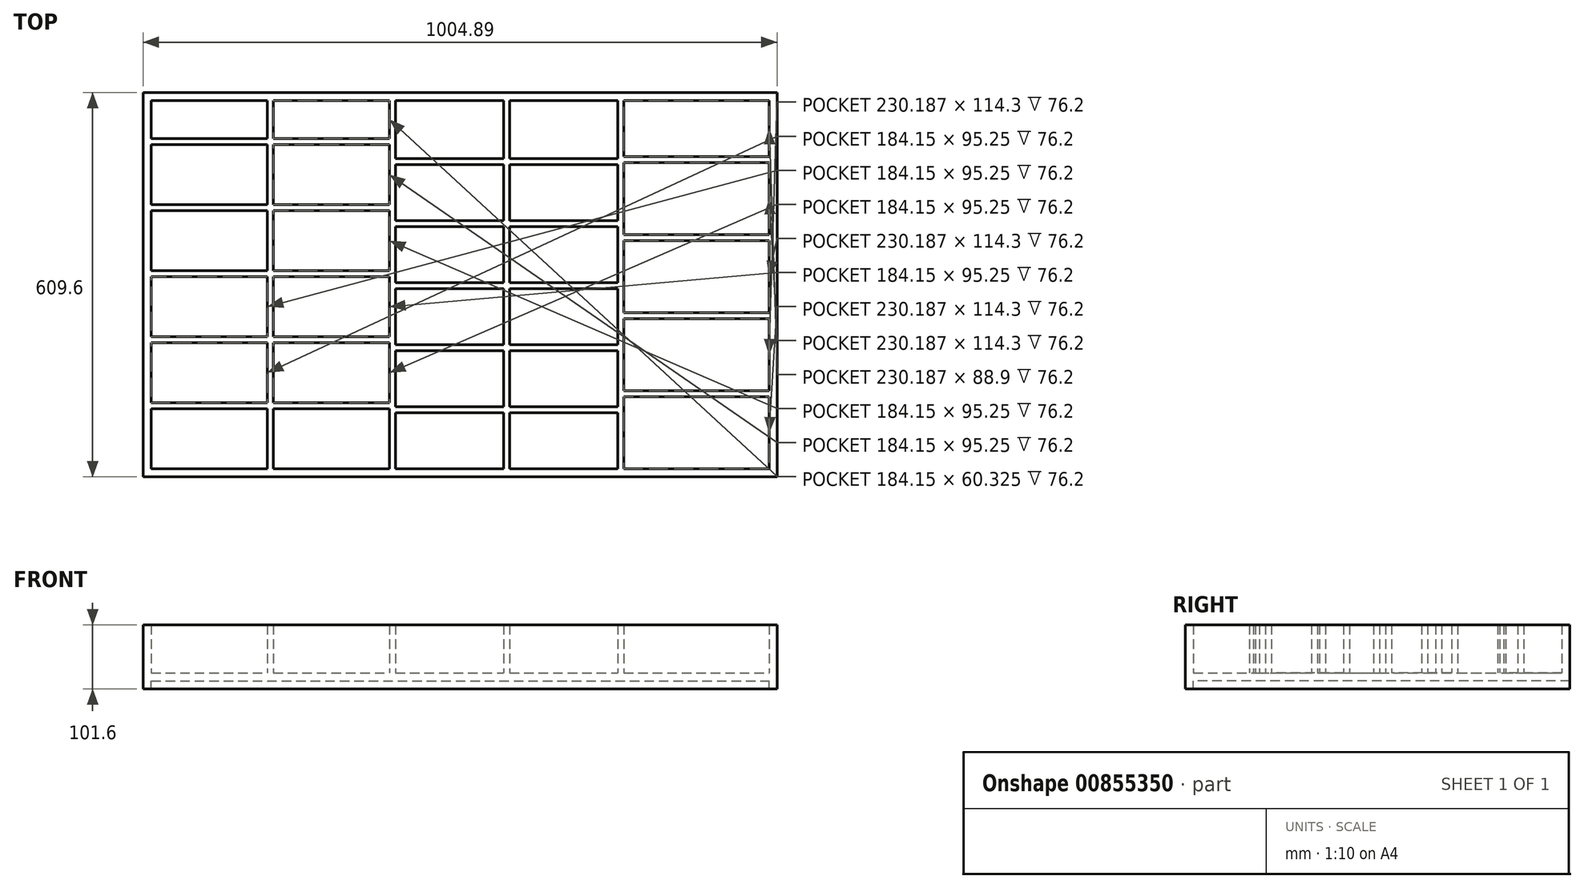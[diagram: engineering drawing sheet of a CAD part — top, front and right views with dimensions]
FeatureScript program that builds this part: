
annotation { "Feature Type Name" : "Feature", "Feature Type Description" : "" }
export const myFeature = defineFeature(function(context is Context, id is Id, definition is map)
    precondition{}
    {
        {
            var Q0;
            Q0=qCreatedBy(makeId("Top.planeOp"),FACE);
            var sketch = newSketch(context, id + "F0", { "sketchPlane" : qUnion([Q0])});
            skLineSegment(sketch, "E0.bottom", {"start": v(-1085.68, 199.34) * mm, "end": v(-901.53, 199.34) * mm});
            skLineSegment(sketch, "E0.top", {"start": v(-1085.68, -384.86) * mm, "end": v(-901.53, -384.86) * mm});
            skLineSegment(sketch, "E0.left", {"start": v(-1085.68, 199.34) * mm, "end": v(-1085.68, 34.24) * mm});
            skLineSegment(sketch, "E0.right", {"start": v(-106.19, 199.34) * mm, "end": v(-106.19, 110.44) * mm});
            skLineSegment(sketch, "E1", {"start": v(-892, -384.86) * mm, "end": v(-892, -289.61) * mm});
            skLineSegment(sketch, "E2", {"start": v(-707.85, -384.86) * mm, "end": v(-707.85, -289.61) * mm});
            skLineSegment(sketch, "E3", {"start": v(-526.88, -384.86) * mm, "end": v(-526.88, -295.96) * mm});
            skLineSegment(sketch, "E4", {"start": v(-345.9, -384.86) * mm, "end": v(-345.9, -295.96) * mm});
            skLineSegment(sketch, "E5.0", {"start": v(-901.53, -384.86) * mm, "end": v(-901.53, -289.61) * mm});
            skLineSegment(sketch, "E6.0", {"start": v(-698.33, -384.86) * mm, "end": v(-698.33, -295.96) * mm});
            skLineSegment(sketch, "E7.0", {"start": v(-517.35, -384.86) * mm, "end": v(-517.35, -295.96) * mm});
            skLineSegment(sketch, "E8.0", {"start": v(-336.38, -384.86) * mm, "end": v(-336.38, -270.56) * mm});
            skLineSegment(sketch, "E9.0", {"start": v(-1098.38, 212.04) * mm, "end": v(-93.49, 212.04) * mm});
            skLineSegment(sketch, "E9.1", {"start": v(-1098.38, 212.04) * mm, "end": v(-1098.38, -397.56) * mm});
            skLineSegment(sketch, "E9.2", {"start": v(-1098.38, -397.56) * mm, "end": v(-93.49, -397.56) * mm});
            skLineSegment(sketch, "E9.3", {"start": v(-93.49, 212.04) * mm, "end": v(-93.49, -397.56) * mm});
            skLineSegment(sketch, "E10", {"start": v(-1085.68, -280.09) * mm, "end": v(-901.53, -280.09) * mm});
            skLineSegment(sketch, "E11", {"start": v(-1085.68, -175.31) * mm, "end": v(-901.53, -175.31) * mm});
            skLineSegment(sketch, "E12", {"start": v(-707.85, -80.06) * mm, "end": v(-892, -80.06) * mm});
            skLineSegment(sketch, "E13", {"start": v(-1085.68, 34.24) * mm, "end": v(-901.53, 34.24) * mm});
            skLineSegment(sketch, "E14", {"start": v(-1085.68, 139.01) * mm, "end": v(-901.53, 139.01) * mm});
            skLineSegment(sketch, "E15", {"start": v(-698.33, -286.44) * mm, "end": v(-526.88, -286.44) * mm});
            skLineSegment(sketch, "E16", {"start": v(-345.9, -197.54) * mm, "end": v(-517.35, -197.54) * mm});
            skLineSegment(sketch, "E17", {"start": v(-698.33, -99.11) * mm, "end": v(-526.88, -99.11) * mm});
            skLineSegment(sketch, "E18", {"start": v(-345.9, -0.69) * mm, "end": v(-517.35, -0.69) * mm});
            skLineSegment(sketch, "E19", {"start": v(-698.33, 107.26) * mm, "end": v(-526.88, 107.26) * mm});
            skLineSegment(sketch, "E20.0", {"start": v(-698.33, 97.74) * mm, "end": v(-526.88, 97.74) * mm});
            skLineSegment(sketch, "E21.0", {"start": v(-345.9, 8.84) * mm, "end": v(-517.35, 8.84) * mm});
            skLineSegment(sketch, "E22.0", {"start": v(-698.33, -89.59) * mm, "end": v(-526.88, -89.59) * mm});
            skLineSegment(sketch, "E23.0", {"start": v(-345.9, -188.01) * mm, "end": v(-517.35, -188.01) * mm});
            skLineSegment(sketch, "E24.0", {"start": v(-698.33, -295.96) * mm, "end": v(-526.88, -295.96) * mm});
            skLineSegment(sketch, "E25.0", {"start": v(-1085.68, -289.61) * mm, "end": v(-901.53, -289.61) * mm});
            skLineSegment(sketch, "E26.0", {"start": v(-1085.68, -184.84) * mm, "end": v(-901.53, -184.84) * mm});
            skLineSegment(sketch, "E27.0", {"start": v(-707.85, -70.54) * mm, "end": v(-892, -70.54) * mm});
            skLineSegment(sketch, "E28.0", {"start": v(-1085.68, 24.71) * mm, "end": v(-901.53, 24.71) * mm});
            skLineSegment(sketch, "E29.0", {"start": v(-1085.68, 129.49) * mm, "end": v(-901.53, 129.49) * mm});
            skLineSegment(sketch, "E30", {"start": v(-336.38, -270.56) * mm, "end": v(-106.19, -270.56) * mm});
            skLineSegment(sketch, "E31", {"start": v(-336.38, -137.21) * mm, "end": v(-106.19, -137.21) * mm});
            skLineSegment(sketch, "E32", {"start": v(-336.38, -13.39) * mm, "end": v(-106.19, -13.39) * mm});
            skLineSegment(sketch, "E33", {"start": v(-106.19, 100.91) * mm, "end": v(-336.38, 100.91) * mm});
            skLineSegment(sketch, "E34.0", {"start": v(-336.38, -261.04) * mm, "end": v(-106.19, -261.04) * mm});
            skLineSegment(sketch, "E35.0", {"start": v(-336.38, -146.74) * mm, "end": v(-106.19, -146.74) * mm});
            skLineSegment(sketch, "E36.0", {"start": v(-336.38, -22.91) * mm, "end": v(-106.19, -22.91) * mm});
            skLineSegment(sketch, "E37.0", {"start": v(-106.19, 110.44) * mm, "end": v(-336.38, 110.44) * mm});
            skLineSegment(sketch, "E38.trimOffspring", {"start": v(-892, 199.34) * mm, "end": v(-707.85, 199.34) * mm});
            skLineSegment(sketch, "E39.trimOffspring", {"start": v(-892, 139.01) * mm, "end": v(-892, 199.34) * mm});
            skLineSegment(sketch, "E40.trimOffspring", {"start": v(-901.53, 139.01) * mm, "end": v(-901.53, 199.34) * mm});
            skLineSegment(sketch, "E41.trimOffspring", {"start": v(-892, 139.01) * mm, "end": v(-707.85, 139.01) * mm});
            skLineSegment(sketch, "E42.trimOffspring", {"start": v(-892, 129.49) * mm, "end": v(-707.85, 129.49) * mm});
            skLineSegment(sketch, "E43.trimOffspring", {"start": v(-1085.68, 24.71) * mm, "end": v(-1085.68, -70.54) * mm});
            skLineSegment(sketch, "E44.trimOffspring", {"start": v(-1085.68, -80.06) * mm, "end": v(-1085.68, -175.31) * mm});
            skLineSegment(sketch, "E45.trimOffspring", {"start": v(-1085.68, -184.84) * mm, "end": v(-1085.68, -280.09) * mm});
            skLineSegment(sketch, "E46.trimOffspring", {"start": v(-1085.68, -289.61) * mm, "end": v(-1085.68, -384.86) * mm});
            skLineSegment(sketch, "E47.trimOffspring", {"start": v(-901.53, 34.24) * mm, "end": v(-901.53, 129.49) * mm});
            skLineSegment(sketch, "E48.trimOffspring", {"start": v(-892, 34.24) * mm, "end": v(-707.85, 34.24) * mm});
            skLineSegment(sketch, "E49.trimOffspring", {"start": v(-892, 34.24) * mm, "end": v(-892, 129.49) * mm});
            skLineSegment(sketch, "E50.trimOffspring", {"start": v(-892, 24.71) * mm, "end": v(-707.85, 24.71) * mm});
            skLineSegment(sketch, "E51.trimOffspring", {"start": v(-901.53, -80.06) * mm, "end": v(-1085.68, -80.06) * mm});
            skLineSegment(sketch, "E52.trimOffspring", {"start": v(-901.53, -70.54) * mm, "end": v(-901.53, 24.71) * mm});
            skLineSegment(sketch, "E53.trimOffspring", {"start": v(-901.53, -70.54) * mm, "end": v(-1085.68, -70.54) * mm});
            skLineSegment(sketch, "E54.trimOffspring", {"start": v(-892, -70.54) * mm, "end": v(-892, 24.71) * mm});
            skLineSegment(sketch, "E55.trimOffspring", {"start": v(-698.33, 107.26) * mm, "end": v(-698.33, 199.34) * mm});
            skLineSegment(sketch, "E56.trimOffspring", {"start": v(-707.85, 139.01) * mm, "end": v(-707.85, 199.34) * mm});
            skLineSegment(sketch, "E57.trimOffspring", {"start": v(-698.33, 199.34) * mm, "end": v(-526.88, 199.34) * mm});
            skLineSegment(sketch, "E58.trimOffspring", {"start": v(-698.33, -89.59) * mm, "end": v(-698.33, -0.69) * mm});
            skLineSegment(sketch, "E59.trimOffspring", {"start": v(-698.33, 8.84) * mm, "end": v(-698.33, 97.74) * mm});
            skLineSegment(sketch, "E60.trimOffspring", {"start": v(-707.85, 34.24) * mm, "end": v(-707.85, 129.49) * mm});
            skLineSegment(sketch, "E61.trimOffspring", {"start": v(-707.85, -70.54) * mm, "end": v(-707.85, 24.71) * mm});
            skLineSegment(sketch, "E62.trimOffspring", {"start": v(-892, -384.86) * mm, "end": v(-707.85, -384.86) * mm});
            skLineSegment(sketch, "E63.trimOffspring", {"start": v(-698.33, -384.86) * mm, "end": v(-526.88, -384.86) * mm});
            skLineSegment(sketch, "E64.trimOffspring", {"start": v(-698.33, -286.44) * mm, "end": v(-698.33, -197.54) * mm});
            skLineSegment(sketch, "E65.trimOffspring", {"start": v(-707.85, -280.09) * mm, "end": v(-707.85, -184.84) * mm});
            skLineSegment(sketch, "E66.trimOffspring", {"start": v(-892, -289.61) * mm, "end": v(-707.85, -289.61) * mm});
            skLineSegment(sketch, "E67.trimOffspring", {"start": v(-892, -280.09) * mm, "end": v(-892, -184.84) * mm});
            skLineSegment(sketch, "E68.trimOffspring", {"start": v(-901.53, -280.09) * mm, "end": v(-901.53, -184.84) * mm});
            skLineSegment(sketch, "E69.trimOffspring", {"start": v(-892, -280.09) * mm, "end": v(-707.85, -280.09) * mm});
            skLineSegment(sketch, "E70.trimOffspring", {"start": v(-892, -175.31) * mm, "end": v(-707.85, -175.31) * mm});
            skLineSegment(sketch, "E71.trimOffspring", {"start": v(-901.53, -175.31) * mm, "end": v(-901.53, -80.06) * mm});
            skLineSegment(sketch, "E72.trimOffspring", {"start": v(-892, -175.31) * mm, "end": v(-892, -80.06) * mm});
            skLineSegment(sketch, "E73.trimOffspring", {"start": v(-892, -184.84) * mm, "end": v(-707.85, -184.84) * mm});
            skLineSegment(sketch, "E74.trimOffspring", {"start": v(-517.35, -384.86) * mm, "end": v(-345.9, -384.86) * mm});
            skLineSegment(sketch, "E75.trimOffspring", {"start": v(-517.35, -295.96) * mm, "end": v(-345.9, -295.96) * mm});
            skLineSegment(sketch, "E76.trimOffspring", {"start": v(-526.88, -286.44) * mm, "end": v(-526.88, -197.54) * mm});
            skLineSegment(sketch, "E77.trimOffspring", {"start": v(-517.35, -286.44) * mm, "end": v(-345.9, -286.44) * mm});
            skLineSegment(sketch, "E78.trimOffspring", {"start": v(-517.35, -286.44) * mm, "end": v(-517.35, -197.54) * mm});
            skLineSegment(sketch, "E79.trimOffspring", {"start": v(-336.38, -384.86) * mm, "end": v(-106.19, -384.86) * mm});
            skLineSegment(sketch, "E80.trimOffspring", {"start": v(-345.9, -286.44) * mm, "end": v(-345.9, -197.54) * mm});
            skLineSegment(sketch, "E81.trimOffspring", {"start": v(-526.88, -197.54) * mm, "end": v(-698.33, -197.54) * mm});
            skLineSegment(sketch, "E82.trimOffspring", {"start": v(-526.88, -188.01) * mm, "end": v(-526.88, -99.11) * mm});
            skLineSegment(sketch, "E83.trimOffspring", {"start": v(-526.88, -188.01) * mm, "end": v(-698.33, -188.01) * mm});
            skLineSegment(sketch, "E84.trimOffspring", {"start": v(-517.35, -188.01) * mm, "end": v(-517.35, -99.11) * mm});
            skLineSegment(sketch, "E85.trimOffspring", {"start": v(-345.9, -188.01) * mm, "end": v(-345.9, -99.11) * mm});
            skLineSegment(sketch, "E86.trimOffspring", {"start": v(-336.38, -261.04) * mm, "end": v(-336.38, -146.74) * mm});
            skLineSegment(sketch, "E87.trimOffspring", {"start": v(-336.38, -137.21) * mm, "end": v(-336.38, -22.91) * mm});
            skLineSegment(sketch, "E88.trimOffspring", {"start": v(-336.38, -13.39) * mm, "end": v(-336.38, 100.91) * mm});
            skLineSegment(sketch, "E89.trimOffspring", {"start": v(-345.9, 8.84) * mm, "end": v(-345.9, 97.74) * mm});
            skLineSegment(sketch, "E90.trimOffspring", {"start": v(-345.9, 107.26) * mm, "end": v(-345.9, 199.34) * mm});
            skLineSegment(sketch, "E91.trimOffspring", {"start": v(-336.38, 110.44) * mm, "end": v(-336.38, 199.34) * mm});
            skLineSegment(sketch, "E92.trimOffspring", {"start": v(-517.35, -99.11) * mm, "end": v(-345.9, -99.11) * mm});
            skLineSegment(sketch, "E93.trimOffspring", {"start": v(-526.88, -89.59) * mm, "end": v(-526.88, -0.69) * mm});
            skLineSegment(sketch, "E94.trimOffspring", {"start": v(-517.35, -89.59) * mm, "end": v(-345.9, -89.59) * mm});
            skLineSegment(sketch, "E95.trimOffspring", {"start": v(-517.35, -89.59) * mm, "end": v(-517.35, -0.69) * mm});
            skLineSegment(sketch, "E96.trimOffspring", {"start": v(-526.88, 8.84) * mm, "end": v(-698.33, 8.84) * mm});
            skLineSegment(sketch, "E97.trimOffspring", {"start": v(-526.88, 8.84) * mm, "end": v(-526.88, 97.74) * mm});
            skLineSegment(sketch, "E98.trimOffspring", {"start": v(-526.88, -0.69) * mm, "end": v(-698.33, -0.69) * mm});
            skLineSegment(sketch, "E99.trimOffspring", {"start": v(-517.35, 8.84) * mm, "end": v(-517.35, 97.74) * mm});
            skLineSegment(sketch, "E100.trimOffspring", {"start": v(-517.35, 107.26) * mm, "end": v(-345.9, 107.26) * mm});
            skLineSegment(sketch, "E101.trimOffspring", {"start": v(-526.88, 107.26) * mm, "end": v(-526.88, 199.34) * mm});
            skLineSegment(sketch, "E102.trimOffspring", {"start": v(-517.35, 97.74) * mm, "end": v(-345.9, 97.74) * mm});
            skLineSegment(sketch, "E103.trimOffspring", {"start": v(-517.35, 107.26) * mm, "end": v(-517.35, 199.34) * mm});
            skLineSegment(sketch, "E104.trimOffspring", {"start": v(-517.35, 199.34) * mm, "end": v(-345.9, 199.34) * mm});
            skLineSegment(sketch, "E105.trimOffspring", {"start": v(-336.38, 199.34) * mm, "end": v(-106.19, 199.34) * mm});
            skLineSegment(sketch, "E106.trimOffspring", {"start": v(-106.19, 100.91) * mm, "end": v(-106.19, -13.39) * mm});
            skLineSegment(sketch, "E107.trimOffspring", {"start": v(-106.19, -22.91) * mm, "end": v(-106.19, -261.04) * mm});
            skLineSegment(sketch, "E108.trimOffspring", {"start": v(-106.19, -270.56) * mm, "end": v(-106.19, -384.86) * mm});
            skLineSegment(sketch, "E109.trimOffspring", {"start": v(-698.33, -188.01) * mm, "end": v(-698.33, -99.11) * mm});
            skLineSegment(sketch, "E110.trimOffspring", {"start": v(-707.85, -175.31) * mm, "end": v(-707.85, -80.06) * mm});
            skLineSegment(sketch, "E111.trimOffspring", {"start": v(-345.9, -89.59) * mm, "end": v(-345.9, -0.69) * mm});
            skSolve(sketch);
        }
        {
            var Q0;
            {var subQ18=sQuery(id+"F0.wireOp",EDGE,"E0.bottom");Q0=makeQuery(id+"F0.imprint","IMPRINT",FACE,{"disambiguationData":[TD([[makeQuery(id+"F0.imprint","IMPRINT",EDGE,{"derivedFrom":subQ18}),1.0]])]});}
            extrude(context, id + "F1", {"entities" : qUnion([Q0]), "depth" : 76.2 * mm, "offsetDistance" : 25.4 * mm});
        }
        {
            var Q0;
            Q0=makeQuery(id+"F1.opExtrude","CAP_FACE",FACE,{"disambiguationData":[OSD([sQuery(id+"F0.wireOp",EDGE,"E0.bottom"),sQuery(id+"F0.wireOp",EDGE,"E0.top"),sQuery(id+"F0.wireOp",EDGE,"E0.left"),sQuery(id+"F0.wireOp",EDGE,"E0.right"),sQuery(id+"F0.wireOp",EDGE,"E1"),sQuery(id+"F0.wireOp",EDGE,"E2"),sQuery(id+"F0.wireOp",EDGE,"E3"),sQuery(id+"F0.wireOp",EDGE,"E4"),sQuery(id+"F0.wireOp",EDGE,"E5.0"),sQuery(id+"F0.wireOp",EDGE,"E6.0"),sQuery(id+"F0.wireOp",EDGE,"E7.0"),sQuery(id+"F0.wireOp",EDGE,"E8.0"),sQuery(id+"F0.wireOp",EDGE,"E9.0"),sQuery(id+"F0.wireOp",EDGE,"E9.1"),sQuery(id+"F0.wireOp",EDGE,"E9.2"),sQuery(id+"F0.wireOp",EDGE,"E9.3"),sQuery(id+"F0.wireOp",EDGE,"E10"),sQuery(id+"F0.wireOp",EDGE,"E11"),sQuery(id+"F0.wireOp",EDGE,"E12"),sQuery(id+"F0.wireOp",EDGE,"E13"),sQuery(id+"F0.wireOp",EDGE,"E14"),sQuery(id+"F0.wireOp",EDGE,"E15"),sQuery(id+"F0.wireOp",EDGE,"E16"),sQuery(id+"F0.wireOp",EDGE,"E17"),sQuery(id+"F0.wireOp",EDGE,"E18"),sQuery(id+"F0.wireOp",EDGE,"E19"),sQuery(id+"F0.wireOp",EDGE,"E20.0"),sQuery(id+"F0.wireOp",EDGE,"E21.0"),sQuery(id+"F0.wireOp",EDGE,"E22.0"),sQuery(id+"F0.wireOp",EDGE,"E23.0"),sQuery(id+"F0.wireOp",EDGE,"E24.0"),sQuery(id+"F0.wireOp",EDGE,"E25.0"),sQuery(id+"F0.wireOp",EDGE,"E26.0"),sQuery(id+"F0.wireOp",EDGE,"E27.0"),sQuery(id+"F0.wireOp",EDGE,"E28.0"),sQuery(id+"F0.wireOp",EDGE,"E29.0"),sQuery(id+"F0.wireOp",EDGE,"E30"),sQuery(id+"F0.wireOp",EDGE,"E31"),sQuery(id+"F0.wireOp",EDGE,"E32"),sQuery(id+"F0.wireOp",EDGE,"E33"),sQuery(id+"F0.wireOp",EDGE,"E34.0"),sQuery(id+"F0.wireOp",EDGE,"E35.0"),sQuery(id+"F0.wireOp",EDGE,"E36.0"),sQuery(id+"F0.wireOp",EDGE,"E37.0"),sQuery(id+"F0.wireOp",EDGE,"E38.trimOffspring"),sQuery(id+"F0.wireOp",EDGE,"E39.trimOffspring"),sQuery(id+"F0.wireOp",EDGE,"E40.trimOffspring"),sQuery(id+"F0.wireOp",EDGE,"E41.trimOffspring"),sQuery(id+"F0.wireOp",EDGE,"E42.trimOffspring"),sQuery(id+"F0.wireOp",EDGE,"E43.trimOffspring"),sQuery(id+"F0.wireOp",EDGE,"E44.trimOffspring"),sQuery(id+"F0.wireOp",EDGE,"E45.trimOffspring"),sQuery(id+"F0.wireOp",EDGE,"E46.trimOffspring"),sQuery(id+"F0.wireOp",EDGE,"E47.trimOffspring"),sQuery(id+"F0.wireOp",EDGE,"E48.trimOffspring"),sQuery(id+"F0.wireOp",EDGE,"E49.trimOffspring"),sQuery(id+"F0.wireOp",EDGE,"E50.trimOffspring"),sQuery(id+"F0.wireOp",EDGE,"E51.trimOffspring"),sQuery(id+"F0.wireOp",EDGE,"E52.trimOffspring"),sQuery(id+"F0.wireOp",EDGE,"E53.trimOffspring"),sQuery(id+"F0.wireOp",EDGE,"E54.trimOffspring"),sQuery(id+"F0.wireOp",EDGE,"E55.trimOffspring"),sQuery(id+"F0.wireOp",EDGE,"E56.trimOffspring"),sQuery(id+"F0.wireOp",EDGE,"E57.trimOffspring"),sQuery(id+"F0.wireOp",EDGE,"E58.trimOffspring"),sQuery(id+"F0.wireOp",EDGE,"E59.trimOffspring"),sQuery(id+"F0.wireOp",EDGE,"E60.trimOffspring"),sQuery(id+"F0.wireOp",EDGE,"E61.trimOffspring"),sQuery(id+"F0.wireOp",EDGE,"E62.trimOffspring"),sQuery(id+"F0.wireOp",EDGE,"E63.trimOffspring"),sQuery(id+"F0.wireOp",EDGE,"E64.trimOffspring"),sQuery(id+"F0.wireOp",EDGE,"E65.trimOffspring"),sQuery(id+"F0.wireOp",EDGE,"E66.trimOffspring"),sQuery(id+"F0.wireOp",EDGE,"E67.trimOffspring"),sQuery(id+"F0.wireOp",EDGE,"E68.trimOffspring"),sQuery(id+"F0.wireOp",EDGE,"E69.trimOffspring"),sQuery(id+"F0.wireOp",EDGE,"E70.trimOffspring"),sQuery(id+"F0.wireOp",EDGE,"E71.trimOffspring"),sQuery(id+"F0.wireOp",EDGE,"E72.trimOffspring"),sQuery(id+"F0.wireOp",EDGE,"E73.trimOffspring"),sQuery(id+"F0.wireOp",EDGE,"E74.trimOffspring"),sQuery(id+"F0.wireOp",EDGE,"E75.trimOffspring"),sQuery(id+"F0.wireOp",EDGE,"E76.trimOffspring"),sQuery(id+"F0.wireOp",EDGE,"E77.trimOffspring"),sQuery(id+"F0.wireOp",EDGE,"E78.trimOffspring"),sQuery(id+"F0.wireOp",EDGE,"E79.trimOffspring"),sQuery(id+"F0.wireOp",EDGE,"E80.trimOffspring"),sQuery(id+"F0.wireOp",EDGE,"E81.trimOffspring"),sQuery(id+"F0.wireOp",EDGE,"E82.trimOffspring"),sQuery(id+"F0.wireOp",EDGE,"E83.trimOffspring"),sQuery(id+"F0.wireOp",EDGE,"E84.trimOffspring"),sQuery(id+"F0.wireOp",EDGE,"E85.trimOffspring"),sQuery(id+"F0.wireOp",EDGE,"E86.trimOffspring"),sQuery(id+"F0.wireOp",EDGE,"E87.trimOffspring"),sQuery(id+"F0.wireOp",EDGE,"E88.trimOffspring"),sQuery(id+"F0.wireOp",EDGE,"E89.trimOffspring"),sQuery(id+"F0.wireOp",EDGE,"E90.trimOffspring"),sQuery(id+"F0.wireOp",EDGE,"E91.trimOffspring"),sQuery(id+"F0.wireOp",EDGE,"E92.trimOffspring"),sQuery(id+"F0.wireOp",EDGE,"E93.trimOffspring"),sQuery(id+"F0.wireOp",EDGE,"E94.trimOffspring"),sQuery(id+"F0.wireOp",EDGE,"E95.trimOffspring"),sQuery(id+"F0.wireOp",EDGE,"E96.trimOffspring"),sQuery(id+"F0.wireOp",EDGE,"E97.trimOffspring"),sQuery(id+"F0.wireOp",EDGE,"E98.trimOffspring"),sQuery(id+"F0.wireOp",EDGE,"E99.trimOffspring"),sQuery(id+"F0.wireOp",EDGE,"E100.trimOffspring"),sQuery(id+"F0.wireOp",EDGE,"E101.trimOffspring"),sQuery(id+"F0.wireOp",EDGE,"E102.trimOffspring"),sQuery(id+"F0.wireOp",EDGE,"E103.trimOffspring"),sQuery(id+"F0.wireOp",EDGE,"E104.trimOffspring"),sQuery(id+"F0.wireOp",EDGE,"E105.trimOffspring"),sQuery(id+"F0.wireOp",EDGE,"E106.trimOffspring"),sQuery(id+"F0.wireOp",EDGE,"E107.trimOffspring"),sQuery(id+"F0.wireOp",EDGE,"E108.trimOffspring")])],"isStart":true});
            var sketch = newSketch(context, id + "F2", { "sketchPlane" : qUnion([Q0])});
            skLineSegment(sketch, "E112", {"start": v(-93.49, 397.56) * mm, "end": v(-93.49, -212.04) * mm});
            skLineSegment(sketch, "E113", {"start": v(-93.49, -212.04) * mm, "end": v(-1098.38, -212.04) * mm});
            skLineSegment(sketch, "E114", {"start": v(-1098.38, -212.04) * mm, "end": v(-1098.38, 397.56) * mm});
            skLineSegment(sketch, "E115", {"start": v(-1098.38, 397.56) * mm, "end": v(-93.49, 397.56) * mm});
            skSolve(sketch);
        }
        {
            var Q0;
            Q0 = qSketchRegion(id + "F2", true);
            extrude(context, id + "F3", {"entities" : qUnion([Q0]), "operationType" : NewBodyOperationType.ADD, "depth" : 12.7 * mm, "offsetDistance" : 25.4 * mm});
        }
        {
            var Q0;
            Q0=makeQuery(id+"F3.opExtrude","CAP_FACE",FACE,{"disambiguationData":[OSD([sQuery(id+"F2.wireOp",EDGE,"E112"),sQuery(id+"F2.wireOp",EDGE,"E113"),sQuery(id+"F2.wireOp",EDGE,"E114"),sQuery(id+"F2.wireOp",EDGE,"E115")])],"isStart":false});
            var sketch = newSketch(context, id + "F4", { "sketchPlane" : qUnion([Q0])});
            skLineSegment(sketch, "E116", {"start": v(-1098.38, -212.04) * mm, "end": v(-1098.38, 397.56) * mm});
            skLineSegment(sketch, "E117", {"start": v(-1098.38, 397.56) * mm, "end": v(-93.49, 397.56) * mm});
            skLineSegment(sketch, "E118", {"start": v(-93.49, 397.56) * mm, "end": v(-93.49, -212.04) * mm});
            skLineSegment(sketch, "E119", {"start": v(-93.49, -212.04) * mm, "end": v(-106.19, -212.04) * mm});
            skLineSegment(sketch, "E120", {"start": v(-106.19, -212.04) * mm, "end": v(-106.19, 384.86) * mm});
            skLineSegment(sketch, "E121", {"start": v(-106.19, 384.86) * mm, "end": v(-1085.68, 384.86) * mm});
            skLineSegment(sketch, "E122", {"start": v(-1085.68, -212.04) * mm, "end": v(-1098.38, -212.04) * mm});
            skLineSegment(sketch, "E123", {"start": v(-1085.68, -212.04) * mm, "end": v(-1085.68, 384.86) * mm});
            skPoint(sketch, "E124.start.orphan", {"position": v(-1098.38, 384.86) * mm});
            skSolve(sketch);
        }
        {
            var Q0;
            Q0=makeQuery(id+"F4.imprint","IMPRINT",FACE,{"disambiguationData":[TD([[makeQuery(id+"F4.imprint","IMPRINT",EDGE,{"derivedFrom":sQuery(id+"F4.wireOp",EDGE,"E116")}),-1.0]])]});
            extrude(context, id + "F5", {"entities" : qUnion([Q0]), "operationType" : NewBodyOperationType.ADD, "depth" : 12.7 * mm, "offsetDistance" : 25.4 * mm});
        }
    });
